# Revit family: 1333xxx Eclipse Round 350 - 3000K
name_source: partatom
category: Lighting Fixtures
units: mm (PartAtom-declared; Revit-internal decimal feet)

## family parameters
Always vertical = Yes
Cut with Voids When Loaded = No
Host = Wall
Light Source = Yes
OmniClass Number = 23.80.70.00
OmniClass Title = Lighting
Part Type = Normal
Room Calculation Point = No
Round Connector Dimension = Use Diameter
Shared = No

## types (2) — shared parameters
Color Filter = 16777215
Dimming Lamp Color Temperature Shift = <None>
Driver Required = No
Electrical Class = 1
Lamp = LED
Length of Cable Supplied = Not Applicable
Light Source Fixed = Yes
Main Finish = Plaster
Main Material = Plaster
Manufacturer = Astro Lighting Ltd
Manufacturer URL - Europe and Rest of World = www.astrolighting.com
Manufacturer URL - North America = us.astrolighting.com
Product CCT = 3000K
Product CRI = 80
Product Dimensions (MM) = Ø350 x 39
Product Location = Wall
Product Name = Eclipse Round 350
Product Weight (KG) = 3.232
Tilt Angle = 60.00°
URL = www.astrolighting.com
zero-valued in all types: Default Elevation

## per-type parameters (varying)
| type | ADA compliant | Dimmable | Dimming Method | Driver Included | Efficacy (lm/w) | Location / IP Rating | Photometric Web File | Power (Watts) | Product SKU |
| CE | N / A | No | Not Applicable | Yes | 41 | IP20 | 1333026 Eclipse Round 350 LED 3000K_Photometry_IES_Iss.01.ies | 16.4 | 1333026 |
| ETL |  | Yes | 0-10V | Yes - Integral | 40 | Interior / Dry | 1333027_Eclipse Round 350 LED_Photometry_IES_Iss.01.ies | 17.6 | 1333027 |

## geometry (parser evidence)
native form markers: Sweep x3
no freeform markers — native parametric forms only
